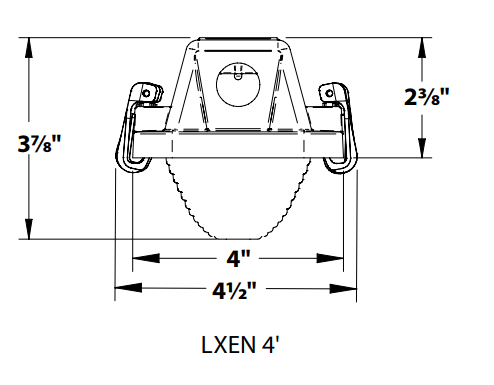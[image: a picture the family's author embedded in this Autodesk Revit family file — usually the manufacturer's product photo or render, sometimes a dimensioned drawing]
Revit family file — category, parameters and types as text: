
# Revit family: LXEN
name_source: partatom
category: Lighting Fixtures
units: mm (PartAtom-declared; Revit-internal decimal feet)

## family parameters
Cut with Voids When Loaded = No
Host = Face
Light Source = Yes
OmniClass Number = 23.80.70.11
OmniClass Title = Luminaries for Internal Lighting
Part Type = Normal
Room Calculation Point = No
Round Connector Dimension = Use Diameter
Shared = Yes

## types (1)
- LXEN
    Apparent Load = 0 VA
    Backbox = White
    Certification = All luminaires are built to UL1598 and 2108
standards, and bear appropriate CSA labels.
Ingress protection IP65, IP66, and IP67 standard.
UL Sanitation Certified per NSF Standards. Wet
location labeling is standard. DLC® (DesignLights
Consortium) Qualified. Please refer to the DLC
website for specific product qualifications at
www.designlights.org. The DTS, Dimming Bypass
Module, is for emergency circuit control loads
including sensors and wireless systems listed to
UL924. See page 3 for wiring diagram. Link to
Dimming Bypass Module Specification sheet.
    Color Filter = 16777215
    Default Elevation = 4.0'
    Description = LXEN is a narrow, multi-functional enclosed LED product which serves rugged to severe conditions as well as food service areas. At only 4-1/2inch wide, LXEN provides a slim, linear profile, which fits easily into confined spaces, provides excellent illumination, and comes standard with the certifications required for rough service environments.
    Dimming Lamp Color Temperature Shift = <None>
    Driver = Fixed Output, 0-10 V Dimming
    Emit from Line Length = 2.0'
    Features = Available in 4' length
Narrow housing design for applications with limited space
Long life 60,000 hour LEDs at L80 for reduced maintenance
Four LED color choices
IP65 and IP67 standard
IP66 all sizes when ordered with standard polyacetal (POM) latches
Fiberglass housing with F1 weatherability rating, standard
Wet label
Gasket is non-porous to ensure seal
Impact modified acrylic lens equivalent to 100% DR
Lens firmly secured with captive tamper resistance ready polyacetal (POM) latches
Stainless steel latching optional
UL Sanitation certified to NSF standards
Includes surface mounting brackets
Operates from -40 ºC to 50 ºC as standard
Removable gear tray electrical access
Optional elevated ambient on most models
UL Sanitation certified to NSF standards
DLC® (DesignLights Consortium) Qualified - see www.designlights.org
Five year warranty (Terms and Conditions apply)
    Glass = White Glass
    Lamp = LED Lamp
    Lumen Output = Extra Low Watt, Low Watt
    Manufacturer = Columbia Lighting
    Model = LXEN
    Nominal Watts = 102 W
    Photometric Note = For more ies file please find the above link
    Photometric Web File = LXEN4-30LW-RFA-EDU.ies
    Row Length = 4.0'
    Shielding = Lineal ribbed frosted acrylic lens
    Tilt Angle = -90.00°
    URL = https://www.currentlighting.com
    Voltage = 120 V
    Warranty = Five year warranty

## geometry (parser evidence)
native form markers: Blend x1, Sweep x3
no freeform markers — native parametric forms only
